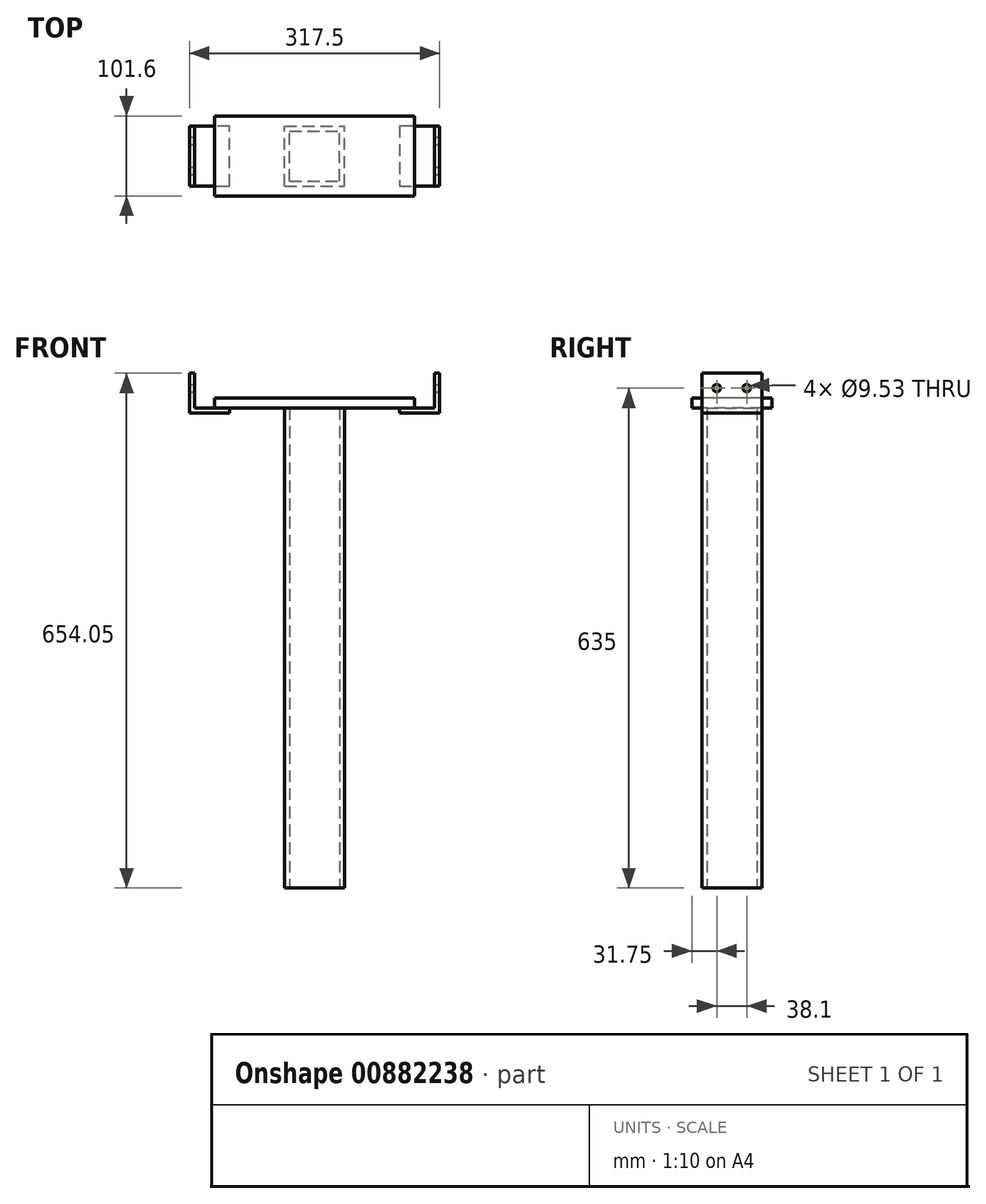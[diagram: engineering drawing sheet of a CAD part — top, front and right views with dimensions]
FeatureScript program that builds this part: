
annotation { "Feature Type Name" : "Feature", "Feature Type Description" : "" }
export const myFeature = defineFeature(function(context is Context, id is Id, definition is map)
    precondition{}
    {
        {
            var Q0;
            Q0=qCreatedBy(makeId("Top.planeOp"),FACE);
            var sketch = newSketch(context, id + "F0", { "sketchPlane" : qUnion([Q0])});
            skLineSegment(sketch, "E0.bottom", {"start": v(0, 0) * mm, "end": v(76.2, 0) * mm});
            skLineSegment(sketch, "E0.top", {"start": v(0, 76.2) * mm, "end": v(76.2, 76.2) * mm});
            skLineSegment(sketch, "E0.left", {"start": v(0, 0) * mm, "end": v(0, 76.2) * mm});
            skLineSegment(sketch, "E0.right", {"start": v(76.2, 0) * mm, "end": v(76.2, 76.2) * mm});
            skLineSegment(sketch, "E1.bottom", {"start": v(6.35, 6.35) * mm, "end": v(69.85, 6.35) * mm});
            skLineSegment(sketch, "E1.top", {"start": v(6.35, 69.85) * mm, "end": v(69.85, 69.85) * mm});
            skLineSegment(sketch, "E1.left", {"start": v(6.35, 6.35) * mm, "end": v(6.35, 69.85) * mm});
            skLineSegment(sketch, "E1.right", {"start": v(69.85, 6.35) * mm, "end": v(69.85, 69.85) * mm});
            skLineSegment(sketch, "E2.bottom", {"start": v(6, 69.85) * mm, "end": v(6.35, 69.85) * mm});
            skLineSegment(sketch, "E2.top", {"start": v(6, 76.2) * mm, "end": v(6.35, 76.2) * mm});
            skSolve(sketch);
        }
        {
            var Q0;
            Q0 = qSketchRegion(id + "F0", true);
            extrude(context, id + "F1", {"entities" : qUnion([Q0]), "depth" : 609.6 * mm, "offsetDistance" : 25.4 * mm});
        }
        {
            var Q0;
            Q0=makeQuery(id+"F1.opExtrude","CAP_FACE",FACE,{"disambiguationData":[OSD([sQuery(id+"F0.wireOp",EDGE,"E0.bottom"),sQuery(id+"F0.wireOp",EDGE,"E0.top"),sQuery(id+"F0.wireOp",EDGE,"E0.left"),sQuery(id+"F0.wireOp",EDGE,"E0.right"),sQuery(id+"F0.wireOp",EDGE,"E1.bottom"),sQuery(id+"F0.wireOp",EDGE,"E1.top"),sQuery(id+"F0.wireOp",EDGE,"E1.left"),sQuery(id+"F0.wireOp",EDGE,"E1.right"),sQuery(id+"F0.wireOp",EDGE,"E2.top")])],"isStart":false});
            var sketch = newSketch(context, id + "F2", { "sketchPlane" : qUnion([Q0])});
            skLineSegment(sketch, "E3.bottom", {"start": v(-88.9, 88.9) * mm, "end": v(165.1, 88.9) * mm});
            skLineSegment(sketch, "E3.top", {"start": v(-88.9, -12.7) * mm, "end": v(165.1, -12.7) * mm});
            skLineSegment(sketch, "E3.left", {"start": v(-88.9, 88.9) * mm, "end": v(-88.9, -12.7) * mm});
            skLineSegment(sketch, "E3.right", {"start": v(165.1, 88.9) * mm, "end": v(165.1, -12.7) * mm});
            skSolve(sketch);
        }
        {
            var Q0;
            Q0 = qSketchRegion(id + "F2", true);
            extrude(context, id + "F3", {"entities" : qUnion([Q0]), "operationType" : NewBodyOperationType.ADD, "depth" : 12.7 * mm, "offsetDistance" : 25.4 * mm});
        }
        {
            var Q0;
            {var subQ0=sQuery(id+"F2.wireOp",EDGE,"E3.top");var subQ1=sQuery(id+"F2.wireOp",EDGE,"E3.left");var subQ2=sQuery(id+"F2.wireOp",EDGE,"E3.bottom");var subQ3=sQuery(id+"F2.wireOp",EDGE,"E3.right");Q0=makeQuery(id+"F3.boolean.opBoolean","SPLIT",FACE,{"disambiguationData":[TD([makeQuery(id+"F1.opExtrude","SWEPT_FACE",FACE,{"disambiguationData":[OSD([sQuery(id+"F0.wireOp",EDGE,"E0.bottom")])]})])],"derivedFrom":makeQuery(id+"F3.opExtrude","CAP_FACE",FACE,{"disambiguationData":[OSD([subQ2,subQ0,subQ1,subQ3])],"isStart":true})});}
            var sketch = newSketch(context, id + "F4", { "sketchPlane" : qUnion([Q0])});
            skLineSegment(sketch, "E4", {"start": v(-88.9, 0) * mm, "end": v(-69.85, 0) * mm});
            skLineSegment(sketch, "E5", {"start": v(-69.85, 0) * mm, "end": v(-69.85, -76.2) * mm});
            skLineSegment(sketch, "E6", {"start": v(-69.85, -76.2) * mm, "end": v(-120.65, -76.2) * mm});
            skLineSegment(sketch, "E7", {"start": v(-120.65, -76.2) * mm, "end": v(-120.65, 0) * mm});
            skLineSegment(sketch, "E8", {"start": v(-120.65, 0) * mm, "end": v(-88.9, 0) * mm});
            skLineSegment(sketch, "E9", {"start": v(146.05, 0) * mm, "end": v(196.85, 0) * mm});
            skLineSegment(sketch, "E10", {"start": v(196.85, 0) * mm, "end": v(196.85, -76.2) * mm});
            skLineSegment(sketch, "E11", {"start": v(196.85, -76.2) * mm, "end": v(146.05, -76.2) * mm});
            skLineSegment(sketch, "E12", {"start": v(146.05, -76.2) * mm, "end": v(146.05, 0) * mm});
            skSolve(sketch);
        }
        {
            var Q0;
            Q0 = qSketchRegion(id + "F4", true);
            extrude(context, id + "F5", {"entities" : qUnion([Q0]), "operationType" : NewBodyOperationType.ADD, "depth" : 6.35 * mm, "offsetDistance" : 25.4 * mm});
        }
        {
            var Q0;
            Q0=makeQuery(id+"F5.opExtrude","CAP_FACE",FACE,{"disambiguationData":[OSD([sQuery(id+"F4.wireOp",EDGE,"E4"),sQuery(id+"F4.wireOp",EDGE,"E5"),sQuery(id+"F4.wireOp",EDGE,"E6"),sQuery(id+"F4.wireOp",EDGE,"E7"),sQuery(id+"F4.wireOp",EDGE,"E8")])],"isStart":true});
            var sketch = newSketch(context, id + "F6", { "sketchPlane" : qUnion([Q0])});
            skLineSegment(sketch, "E13", {"start": v(-120.65, 0) * mm, "end": v(-114.3, 0) * mm});
            skLineSegment(sketch, "E14", {"start": v(-114.3, 0) * mm, "end": v(-114.3, 76.2) * mm});
            skLineSegment(sketch, "E15", {"start": v(-114.3, 76.2) * mm, "end": v(-120.65, 76.2) * mm});
            skLineSegment(sketch, "E16", {"start": v(-120.65, 76.2) * mm, "end": v(-120.65, -1.63) * mm});
            skSolve(sketch);
        }
        {
            var Q0;
            Q0 = qSketchRegion(id + "F6", true);
            extrude(context, id + "F7", {"entities" : qUnion([Q0]), "operationType" : NewBodyOperationType.ADD, "depth" : 44.45 * mm, "offsetDistance" : 25.4 * mm});
        }
        {
            var Q0;
            Q0=makeQuery(id+"F5.opExtrude","CAP_FACE",FACE,{"disambiguationData":[OSD([sQuery(id+"F4.wireOp",EDGE,"E9"),sQuery(id+"F4.wireOp",EDGE,"E10"),sQuery(id+"F4.wireOp",EDGE,"E11"),sQuery(id+"F4.wireOp",EDGE,"E12")])],"isStart":true});
            var sketch = newSketch(context, id + "F8", { "sketchPlane" : qUnion([Q0])});
            skLineSegment(sketch, "E17", {"start": v(196.85, 76.2) * mm, "end": v(190.5, 76.2) * mm});
            skLineSegment(sketch, "E18", {"start": v(190.5, 76.2) * mm, "end": v(190.5, 0) * mm});
            skLineSegment(sketch, "E19", {"start": v(190.5, 0) * mm, "end": v(196.85, 0) * mm});
            skLineSegment(sketch, "E20", {"start": v(196.85, 0) * mm, "end": v(196.85, 76.2) * mm});
            skSolve(sketch);
        }
        {
            var Q0;
            Q0 = qSketchRegion(id + "F8", true);
            extrude(context, id + "F9", {"entities" : qUnion([Q0]), "operationType" : NewBodyOperationType.ADD, "depth" : 44.45 * mm, "offsetDistance" : 25.4 * mm});
        }
        {
            var Q0;
            Q0=makeQuery(id+"F9.boolean.opBoolean","MERGE",FACE,{"derivedFrom":[makeQuery(id+"F5.opExtrude","SWEPT_FACE",FACE,{"disambiguationData":[OSD([sQuery(id+"F4.wireOp",EDGE,"E10")])]}),makeQuery(id+"F9.opExtrude","SWEPT_FACE",FACE,{"disambiguationData":[OSD([sQuery(id+"F8.wireOp",EDGE,"E20")])]})]});
            var sketch = newSketch(context, id + "F10", { "sketchPlane" : qUnion([Q0])});
            skCircle(sketch, "E21", {"center": v(19.05, 635) * mm, "radius": 4.76 * mm});
            skCircle(sketch, "E22", {"center": v(57.15, 635) * mm, "radius": 4.76 * mm});
            skSolve(sketch);
        }
        {
            var Q0;
            Q0 = qSketchRegion(id + "F10", true);
            extrude(context, id + "F11", {"entities" : qUnion([Q0]), "operationType" : NewBodyOperationType.REMOVE, "oppositeDirection" : true, "depth" : 381 * mm, "offsetDistance" : 25.4 * mm});
        }
    });
